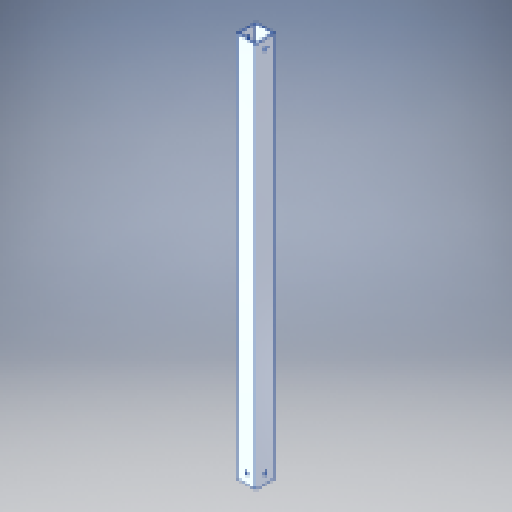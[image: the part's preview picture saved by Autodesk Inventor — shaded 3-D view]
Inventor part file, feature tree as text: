
AUTODESK INVENTOR PART (.ipt)
format: ipt  version: 2024.2 (Build 282272000, 272)  size: 164,864 bytes
history: native  units: in
note: dims shown in document units (in); Inventor stores cm internally (conversion verified against a paired STEP export)
features: extrude x3, sketch x3, other x1
ambient origin geometry x8: Origin, YZ Plane, XZ Plane, XY Plane, X Axis, Y Axis, Z Axis, Center Point
bodies: Solid1 (feature_tree)
feature tree (7):
  extrude  "Extrusion1"  Depth=1.0in TaperAngle=0.0deg
  extrude  "Extrusion2"  Depth=1.0in TaperAngle=0.0deg
  extrude  "Extrusion3"  [1 undecoded]
  sketch  "Sketch1"  dims[d0=0.25in d1=1.0in d2=0.0in]
  sketch  "Sketch2"  dims[d3=1.0in d4=0.0in d5=1.0in d6=0.0in]
  sketch  "Sketch3"
  other  "Cut-Extrude2"
note: 1 required parameter value undecoded (feature->parameter linkage not recoverable at this tier; creation-order binding heuristic only, values carry confidence <= 0.55)
